# Revit family: IS_Ventuno_T6637_BIM_GB
name_source: partatom
category: Plumbing Fixtures
revit_build: Autodesk Revit MEP 2014 (Build: 20130308_1515(x64)
units: mm (PartAtom-declared; Revit-internal decimal feet)

## types (1)
- T663701 - Ventuno Sear & Cover
    Accessories = www.idealspec.co.uk
    AreaUnits = millimeters
    Assembly Code = C1030200
    AssetType = Fixed
    BIMObjectName = ISI_IdealStandard_WCSeatsAndCovers_Ventuno_T6637
    BarCode = 8014140343875
    Brand = Ideal Standard
    CWFU = 0
    ConnectionType = Plumbing
    Cost = 0 $
    Default Elevation = 500 mm  [stored 1.64042 ft]
    Description = Ventuno seat and cover for back to wall and wall mounted WC pan
    DurationUnit = year
    ECA = No
    ExpectedLife = 15
    Features = Seat and cover for back to wall and wall mounted wc pan
    Finish = White
    HWFU = 0
    Help = www.idealspec.co.uk/contact-us.html
    IfcExportAs = IfcSanitaryTerminalType
    IfcExportType = WCSEAT
    InstallationInstructions = www.idealspec.co.uk/resources.html
    LinearUnits = millimeters
    ManufacturerURL = www.idealspec.co.uk
    Model = T663701
    NBSDescription = WC seats and covers
    NBSReference = 45-35-70/391
    Name = WCSeatsAndCovers_Ventuno_T6637_IdealStandard
    NettWeight = 2.7 Kg
    NominalDepth = 445 mm
    NominalHeight = 45 mm
    NominalLength = 0 mm  [stored 0 ft]
    NominalWidth = 360 mm
    PanColor = White
    PanMaterial = Vitreous china
    PanMounting = BackToWall
    ProductInformation = www.idealspec.co.uk/assets/datasheet/T663701
    Shape = Sculptured
    Size = 445 x 45 x 361 mm
    Space = Internal
    SpilloverLevel = 0 mm  [stored 0 ft]
    ToiletPanType = WashDown
    ToiletType = Other
    URL = www.idealspec.co.uk
    Uniclass2015Code = Pr_40_20_93_95
    Uniclass2015Title = WC seats and covers
    Uniclass2015Version = Products v1.1
    Version = 1
    VolumeUnits = Litres
    WFU = 0
    WarrantyDescription = Manufacturers Warranty
    WarrantyDurationParts = 99
    WarrantyDurationUnit = year

note: [stored X ft] marks values corroborated as IEEE doubles in the binary element streams (Revit-internal decimal feet)

## geometry (parser evidence)
native form markers: Sweep x4
no freeform markers — native parametric forms only
